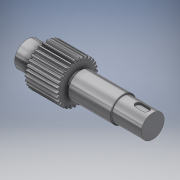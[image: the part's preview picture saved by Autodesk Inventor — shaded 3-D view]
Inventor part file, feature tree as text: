
AUTODESK INVENTOR PART (.ipt)
format: ipt  version: 2018.2 (Build 222227000, 227)  size: 333,312 bytes
history: native  units: in
note: dims shown in document units (in); Inventor stores cm internally (conversion verified against a paired STEP export)
features: sketch x5, revolve x2, plane x2, pattern_circular x2, extrude x2, thread x1, hole x1, chamfer x1
ambient origin geometry x8: Origin, YZ Plane, XZ Plane, XY Plane, X Axis, Y Axis, Z Axis, Center Point
bodies: Solid1 (feature_tree), Solid2 (feature_tree)
feature tree (16):
  revolve  "Revolution1"  [1 undecoded]
  thread  "Thread1"  [1 undecoded]
  plane  "Work Plane1"
  hole  "Hole1"  [1 undecoded]
  pattern_circular  "Circular Pattern1"  Count=3 Angle=360.0deg
  chamfer  "Chamfer1"  Distance=0.0787in Angle=45.0deg
  revolve  "Revolution2"  [1 undecoded]
  extrude  "Extrusion1"  TaperAngle=90.0deg  [1 undecoded]
  pattern_circular  "Circular Pattern2"  [2 undecoded]
  plane  "Work Plane2"
  extrude  "Extrusion2"  Depth=0.3937in
  sketch  "Sketch1"  dims[d0=3.937in d1=2.7559in d2=0.9449in]
  sketch  "Sketch2"  dims[d3=0.7087in d4=1.5748in]
  sketch  "Sketch3"  dims[d5=90.0deg]
  sketch  "Sketch4"  dims[d6=0.3937in d7=0.0in]
  sketch  "Sketch5"  dims[d8=0.3937in d9=0.2362in d10=0.1575in d11=0.0787in d12=90.0deg d13=0.315in d14=0.0in d15=1.1811in d16=360.0deg d18=0.0787in d19=0.0787in d20=45.0deg d21=1.5748in d22=0.8661in d23=0.2362in d24=1.9685in d25=0.2362in d26=2.5984in d27=1.811in d28=1.2598in d29=2.5197in d30=1.5748in d31=1.4173in d33=2.0866in d34=90.0deg d35=2.1654in d37=0.0984in d38=0.0984in d39=0.0295in d40=0.0295in d41=0.4626in d42=0.3937in d43=0.0in d44=11.811in d45=360.0deg d47=0.4724in d48=0.3937in d49=0.3937in d50=0.1378in d51=0.0in]
note: 7 required parameter values undecoded (feature->parameter linkage not recoverable at this tier; creation-order binding heuristic only, values carry confidence <= 0.55)